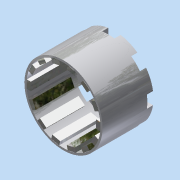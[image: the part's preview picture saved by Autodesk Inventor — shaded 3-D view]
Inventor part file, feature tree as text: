
AUTODESK INVENTOR PART (.ipt)
format: ipt  version: 2015 (Build 190159000, 159)  size: 406,528 bytes
history: native  units: in
note: dims shown in document units (in); Inventor stores cm internally (conversion verified against a paired STEP export)
features: other x4, sketch x3, extrude x2, pattern_circular x2, revolve x1, plane x1, projected_geometry x1
ambient origin geometry x8: Origin, YZ Plane, XZ Plane, XY Plane, X Axis, Y Axis, Z Axis, Center Point
bodies: Solid1 (feature_tree), Solid2 (feature_tree)
feature tree (14):
  other  "Stator.ipt"
  revolve  "Revolution1"  [1 undecoded]
  plane  "Work Plane1"
  extrude  "Extrusion1"  Depth=0.0625in
  pattern_circular  "Circular Pattern1"  [2 undecoded]
  extrude  "Extrusion2"  Depth=0.25in
  pattern_circular  "Circular Pattern2"  [2 undecoded]
  other  "TaggingFeature1"
  sketch  "Sketch1"  dims[d0=0.3937in d1=0.2953in]
  sketch  "Sketch2"  dims[d2=0.1447in d3=0.0625in]
  sketch  "Sketch3"  dims[d4=0.125in d5=0.0625in d6=0.25in d7=0.0625in d8=90.0deg d9=0.125in d10=0.25in d11=1.0in d12=0.0in d13=5.5118in d14=360.0deg d16=0.25in d17=0.375in d18=0.6in d19=1.5748in d21=360.0deg d23=0.375in d24=45.0deg d25=0.25in d26=1.5748in d28=360.0deg d30=0.1875in d31=0.0in d32=1.5748in d33=360.0deg]
  projected_geometry  "Projected Loop2"
  other  "Solid1::Stator.ipt"
  other  "Srf1"
note: 5 required parameter values undecoded (feature->parameter linkage not recoverable at this tier; creation-order binding heuristic only, values carry confidence <= 0.55)